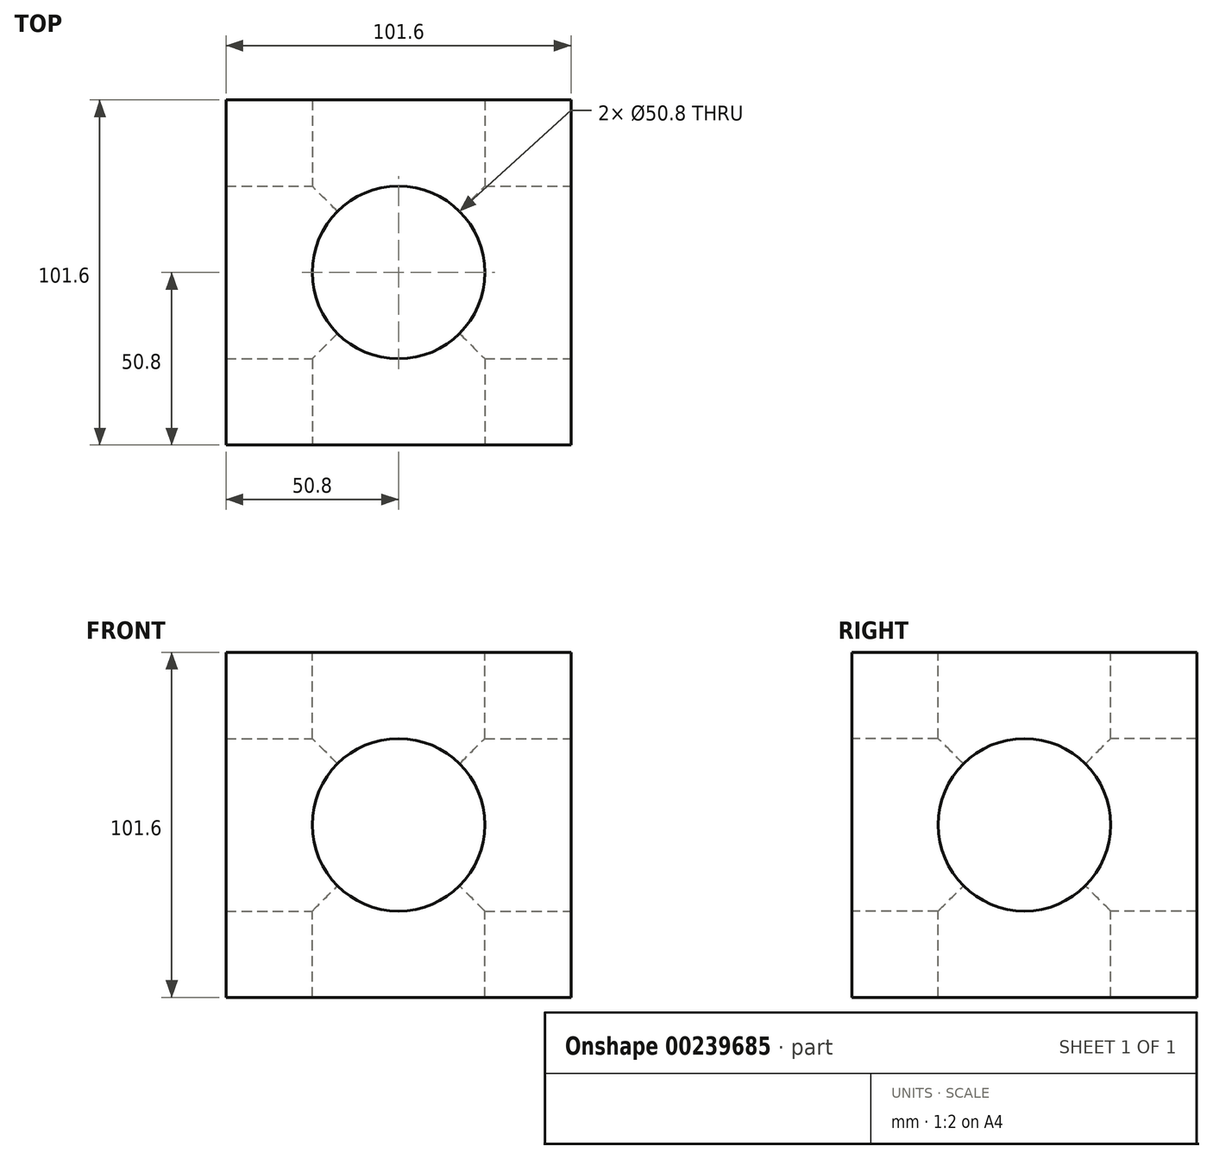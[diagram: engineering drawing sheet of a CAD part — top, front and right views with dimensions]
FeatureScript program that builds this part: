
annotation { "Feature Type Name" : "Feature", "Feature Type Description" : "" }
export const myFeature = defineFeature(function(context is Context, id is Id, definition is map)
    precondition{}
    {
        {
            var Q0;
            Q0=qCreatedBy(makeId("Front.planeOp"),FACE);
            var sketch = newSketch(context, id + "F0", { "sketchPlane" : qUnion([Q0])});
            skLineSegment(sketch, "E0.bottom", {"start": v(50.8, 50.8) * mm, "end": v(-50.8, 50.8) * mm});
            skLineSegment(sketch, "E0.top", {"start": v(50.8, -50.8) * mm, "end": v(-50.8, -50.8) * mm});
            skLineSegment(sketch, "E0.left", {"start": v(50.8, 50.8) * mm, "end": v(50.8, -50.8) * mm});
            skLineSegment(sketch, "E0.right", {"start": v(-50.8, 50.8) * mm, "end": v(-50.8, -50.8) * mm});
            skPoint(sketch, "E0.middle", {"position": v(0, 0) * mm});
            skSolve(sketch);
        }
        {
            var Q0;
            Q0 = qSketchRegion(id + "F0", true);
            extrude(context, id + "F1", {"entities" : qUnion([Q0]), "endBound" : BoundingType.SYMMETRIC, "depth" : 101.6 * mm});
        }
        {
            var Q0;
            Q0=makeQuery(id+"F1.opExtrude","CAP_FACE",FACE,{"disambiguationData":[OSD([sQuery(id+"F0.wireOp",EDGE,"E0.bottom"),sQuery(id+"F0.wireOp",EDGE,"E0.top"),sQuery(id+"F0.wireOp",EDGE,"E0.left"),sQuery(id+"F0.wireOp",EDGE,"E0.right")])],"isStart":false});
            var sketch = newSketch(context, id + "F2", { "sketchPlane" : qUnion([Q0])});
            skCircle(sketch, "E1", {"center": v(0, 0) * mm, "radius": 25.4 * mm});
            skSolve(sketch);
        }
        {
            var Q0;
            Q0 = qSketchRegion(id + "F2", true);
            extrude(context, id + "F3", {"entities" : qUnion([Q0]), "operationType" : NewBodyOperationType.REMOVE, "endBound" : BoundingType.THROUGH_ALL, "oppositeDirection" : true, "depth" : 25.4 * mm});
        }
        {
            var Q0;
            Q0=makeQuery(id+"F1.opExtrude","SWEPT_FACE",FACE,{"disambiguationData":[OSD([sQuery(id+"F0.wireOp",EDGE,"E0.left")])]});
            var sketch = newSketch(context, id + "F4", { "sketchPlane" : qUnion([Q0])});
            skCircle(sketch, "E2", {"center": v(0, 0) * mm, "radius": 25.4 * mm});
            skSolve(sketch);
        }
        {
            var Q0;
            Q0 = qSketchRegion(id + "F4", true);
            extrude(context, id + "F5", {"entities" : qUnion([Q0]), "operationType" : NewBodyOperationType.REMOVE, "endBound" : BoundingType.THROUGH_ALL, "oppositeDirection" : true, "depth" : 25.4 * mm});
        }
        {
            var Q0;
            Q0=makeQuery(id+"F1.opExtrude","SWEPT_FACE",FACE,{"disambiguationData":[OSD([sQuery(id+"F0.wireOp",EDGE,"E0.bottom")])]});
            var sketch = newSketch(context, id + "F6", { "sketchPlane" : qUnion([Q0])});
            skCircle(sketch, "E3", {"center": v(0, 0) * mm, "radius": 25.4 * mm});
            skSolve(sketch);
        }
        {
            var Q0;
            Q0=makeQuery(id+"F6.imprint","IMPRINT",FACE,{"disambiguationData":[TD([[makeQuery(id+"F6.imprint","IMPRINT",EDGE,{"derivedFrom":sQuery(id+"F6.wireOp",EDGE,"E3")}),1.0]])]});
            extrude(context, id + "F7", {"entities" : qUnion([Q0]), "operationType" : NewBodyOperationType.REMOVE, "endBound" : BoundingType.THROUGH_ALL, "oppositeDirection" : true, "depth" : 25.4 * mm});
        }
    });
